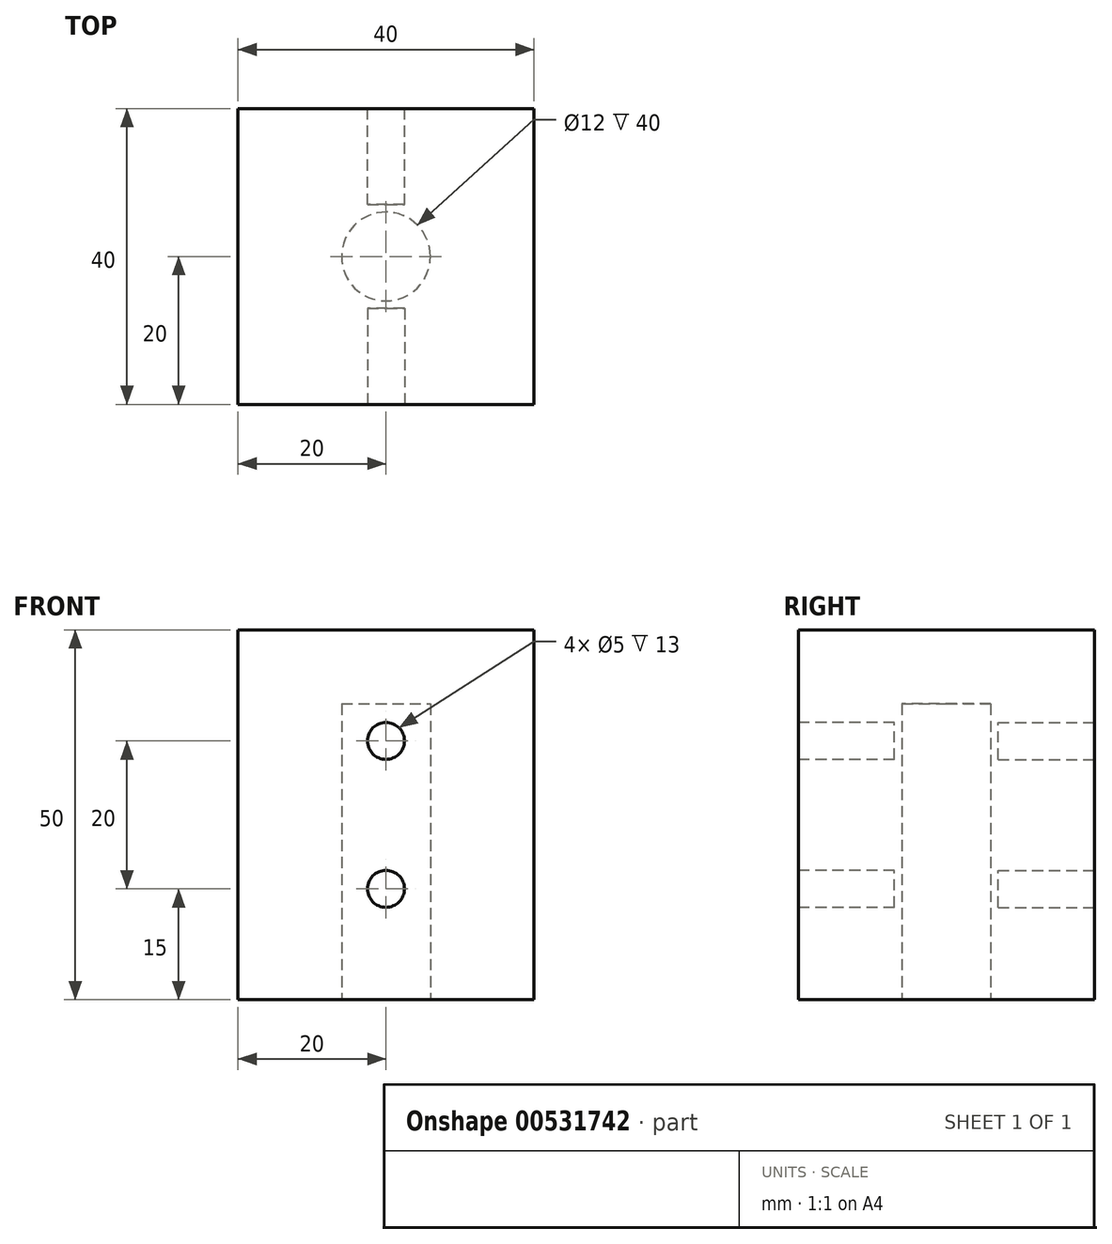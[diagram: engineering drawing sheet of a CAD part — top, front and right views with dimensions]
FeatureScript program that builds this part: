
annotation { "Feature Type Name" : "Feature", "Feature Type Description" : "" }
export const myFeature = defineFeature(function(context is Context, id is Id, definition is map)
    precondition{}
    {
        {
            var Q0;
            Q0=qCreatedBy(makeId("Top.planeOp"),FACE);
            var sketch = newSketch(context, id + "F0", { "sketchPlane" : qUnion([Q0])});
            skLineSegment(sketch, "E0.bottom", {"start": v(20, 20) * mm, "end": v(-20, 20) * mm});
            skLineSegment(sketch, "E0.top", {"start": v(20, -20) * mm, "end": v(-20, -20) * mm});
            skLineSegment(sketch, "E0.left", {"start": v(20, 20) * mm, "end": v(20, -20) * mm});
            skLineSegment(sketch, "E0.right", {"start": v(-20, 20) * mm, "end": v(-20, -20) * mm});
            skPoint(sketch, "E0.middle", {"position": v(0, 0) * mm});
            skSolve(sketch);
        }
        {
            var Q0;
            Q0=makeQuery(id+"F0.imprint","IMPRINT",FACE,{"disambiguationData":[TD([[makeQuery(id+"F0.imprint","IMPRINT",EDGE,{"derivedFrom":sQuery(id+"F0.wireOp",EDGE,"E0.bottom")}),1.0]])]});
            extrude(context, id + "F1", {"entities" : qUnion([Q0]), "depth" : 50 * mm, "offsetDistance" : 25 * mm});
        }
        {
            var Q0;
            Q0=makeQuery(id+"F1.opExtrude","CAP_FACE",FACE,{"disambiguationData":[OSD([sQuery(id+"F0.wireOp",EDGE,"E0.bottom"),sQuery(id+"F0.wireOp",EDGE,"E0.top"),sQuery(id+"F0.wireOp",EDGE,"E0.left"),sQuery(id+"F0.wireOp",EDGE,"E0.right")])],"isStart":true});
            var sketch = newSketch(context, id + "F2", { "sketchPlane" : qUnion([Q0])});
            skCircle(sketch, "E1", {"center": v(0, 0) * mm, "radius": 6 * mm});
            skSolve(sketch);
        }
        {
            var Q0;
            Q0=makeQuery(id+"F2.imprint","IMPRINT",FACE,{"disambiguationData":[TD([[makeQuery(id+"F2.imprint","IMPRINT",EDGE,{"derivedFrom":sQuery(id+"F2.wireOp",EDGE,"E1")}),1.0]])]});
            extrude(context, id + "F3", {"entities" : qUnion([Q0]), "operationType" : NewBodyOperationType.REMOVE, "oppositeDirection" : true, "depth" : 40 * mm, "offsetDistance" : 25 * mm});
        }
        {
            var Q0;
            Q0=makeQuery(id+"F1.opExtrude","SWEPT_FACE",FACE,{"disambiguationData":[OSD([sQuery(id+"F0.wireOp",EDGE,"E0.top")])]});
            var sketch = newSketch(context, id + "F4", { "sketchPlane" : qUnion([Q0])});
            skLineSegment(sketch, "E2", {"start": v(0, 50) * mm, "end": v(0, 35) * mm});
            skLineSegment(sketch, "E3", {"start": v(0, 0) * mm, "end": v(0, 15) * mm});
            skCircle(sketch, "E4", {"center": v(0, 35) * mm, "radius": 2.5 * mm});
            skCircle(sketch, "E5", {"center": v(0, 15) * mm, "radius": 2.5 * mm});
            skSolve(sketch);
        }
        {
            var Q0;
            Q0=makeQuery(id+"F4.imprint","IMPRINT",FACE,{"disambiguationData":[TD([[makeQuery(id+"F4.imprint","IMPRINT",EDGE,{"derivedFrom":sQuery(id+"F4.wireOp",EDGE,"E4")}),1.0]])]});
            var Q1;
            Q1=makeQuery(id+"F4.imprint","IMPRINT",FACE,{"disambiguationData":[TD([[makeQuery(id+"F4.imprint","IMPRINT",EDGE,{"derivedFrom":sQuery(id+"F4.wireOp",EDGE,"E5")}),1.0]])]});
            extrude(context, id + "F5", {"entities" : qUnion([Q0, Q1]), "operationType" : NewBodyOperationType.REMOVE, "oppositeDirection" : true, "depth" : 13 * mm, "offsetDistance" : 25 * mm});
        }
        {
            var Q0;
            Q0=makeQuery(id+"F1.opExtrude","SWEPT_FACE",FACE,{"disambiguationData":[OSD([sQuery(id+"F0.wireOp",EDGE,"E0.bottom")])]});
            extrude(context, id + "F6", {"entities" : qUnion([Q0]), "operationType" : NewBodyOperationType.REMOVE, "oppositeDirection" : true, "depth" : 20 * mm, "offsetDistance" : 25 * mm});
        }
        {
            var Q0;
            Q0=makeQuery(id+"F1.opExtrude","SWEPT_BODY",BODY,{"disambiguationData":[OSD([sQuery(id+"F0.wireOp",EDGE,"E0.bottom"),sQuery(id+"F0.wireOp",EDGE,"E0.top"),sQuery(id+"F0.wireOp",EDGE,"E0.left"),sQuery(id+"F0.wireOp",EDGE,"E0.right")])]});
            var Q1;
            Q1=qCreatedBy(makeId("Front.planeOp"),FACE);
            mirror(context, id + "F7", {"operationType" : NewBodyOperationType.ADD, "entities" : qUnion([Q0]), "mirrorPlane" : qUnion([Q1])});
        }
    });
